# Revit family: BuzziSurf
name_source: partatom
category: Lighting Fixtures
revit_build: Autodesk Revit 2018 (Build: 20190510_1515(x64)
units: mm (PartAtom-declared; Revit-internal decimal feet)

## family parameters
Always vertical = Yes
Cut with Voids When Loaded = No
Host = Ceiling
Light Source = No
Part Type = Normal
Room Calculation Point = No
Round Connector Dimension = Use Diameter
Shared = No

## types (6) — shared parameters
Ceiling Suspended Straight = Yes

## per-type parameters (varying)
| type | Canopy Width | Large Visibility | Light Spacing | Quintet Light Visibility | Solo Visibility | Spot Light | Trio Light Visibility | Width |
| Sol Solo Spot | 12.5 cm | No | 37.5 cm | No | Yes | Yes | No | 108 cm |
| Sol Solo Globe | 12.5 cm | No | 37.5 cm | No | Yes | No | No | 108 cm |
| Sol Trio Globe | 35 cm | Yes | 40 cm | No | No | No | Yes | 140 cm |
| Sol Trio Spot | 35 cm | Yes | 40 cm | No | No | Yes | Yes | 140 cm |
| Sol Quintet Globe | 45 cm | Yes | 37.5 cm | Yes | No | No | Yes | 210 cm |
| Sol Quintet Spot | 45 cm | Yes | 37.5 cm | Yes | No | Yes | Yes | 210 cm |

## geometry (parser evidence)
native form markers: Sweep x10
no freeform markers — native parametric forms only
